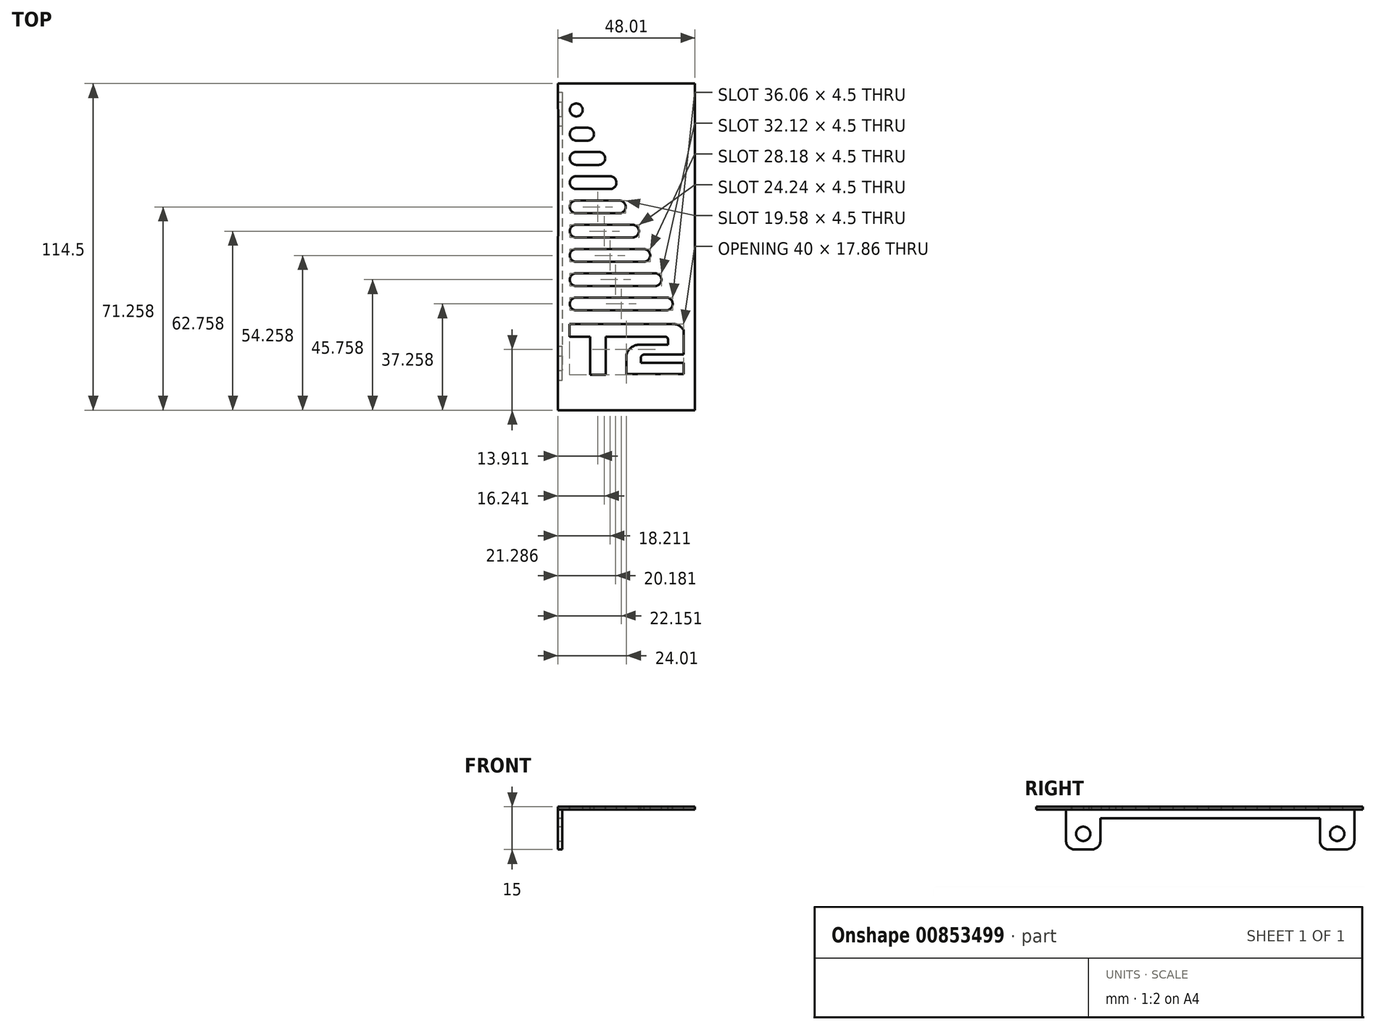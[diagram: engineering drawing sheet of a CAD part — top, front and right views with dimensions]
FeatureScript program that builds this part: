
annotation { "Feature Type Name" : "Feature", "Feature Type Description" : "" }
export const myFeature = defineFeature(function(context is Context, id is Id, definition is map)
    precondition{}
    {
        {
            var Q0;
            Q0=qCreatedBy(makeId("Top.planeOp"),FACE);
            var sketch = newSketch(context, id + "F0", { "sketchPlane" : qUnion([Q0])});
            skLineSegment(sketch, "E0.bottom", {"start": v(-24, 57.25) * mm, "end": v(24, 57.25) * mm});
            skLineSegment(sketch, "E0.right", {"start": v(24, 57.25) * mm, "end": v(24, -57.25) * mm});
            skPoint(sketch, "E0.middle", {"position": v(0, 0) * mm});
            skLineSegment(sketch, "E1", {"start": v(-20, -27.03) * mm, "end": v(-20, -31.53) * mm});
            skLineSegment(sketch, "E2", {"start": v(-12.75, -31.53) * mm, "end": v(-20, -31.53) * mm});
            skLineSegment(sketch, "E3", {"start": v(-12.75, -31.53) * mm, "end": v(-12.75, -44.9) * mm});
            skLineSegment(sketch, "E4", {"start": v(-12.75, -44.9) * mm, "end": v(-7.25, -44.9) * mm});
            skLineSegment(sketch, "E5", {"start": v(19.99, -40.62) * mm, "end": v(4.99, -40.62) * mm});
            skArc(sketch, "E6", {"start": v(4.33, -34.3) * mm, "mid": v(1.6, -35.34) * mm, "end": v(0, -37.8) * mm});
            skArc(sketch, "E7", {"start": v(6.16, -37.76) * mm, "mid": v(5.44, -38.04) * mm, "end": v(4.99, -38.66) * mm});
            skArc(sketch, "E8", {"start": v(20, -29.26) * mm, "mid": v(18.38, -27.56) * mm, "end": v(16.1, -27.03) * mm});
            skLineSegment(sketch, "E9", {"start": v(-20, -27.03) * mm, "end": v(16.1, -27.03) * mm});
            skLineSegment(sketch, "E10", {"start": v(4.99, -38.66) * mm, "end": v(4.99, -40.62) * mm});
            skLineSegment(sketch, "E11", {"start": v(6.16, -37.76) * mm, "end": v(20, -37.76) * mm});
            skLineSegment(sketch, "E12", {"start": v(20, -29.26) * mm, "end": v(20, -37.76) * mm});
            skLineSegment(sketch, "E13", {"start": v(4.33, -34.3) * mm, "end": v(14.5, -34.3) * mm});
            skLineSegment(sketch, "E14", {"start": v(-17.64, -22.24) * mm, "end": v(13.92, -22.24) * mm});
            skLineSegment(sketch, "E15", {"start": v(13.92, -17.74) * mm, "end": v(-17.64, -17.74) * mm});
            skArc(sketch, "E16", {"start": v(-17.64, -17.74) * mm, "mid": v(-19.89, -20) * mm, "end": v(-17.64, -22.24) * mm});
            skArc(sketch, "E17", {"start": v(13.92, -17.74) * mm, "mid": v(16.17, -20) * mm, "end": v(13.92, -22.24) * mm});
            skLineSegment(sketch, "E18", {"start": v(-17.64, -13.74) * mm, "end": v(9.98, -13.74) * mm});
            skLineSegment(sketch, "E19", {"start": v(9.98, -9.24) * mm, "end": v(-17.64, -9.24) * mm});
            skArc(sketch, "E20", {"start": v(-17.64, -9.24) * mm, "mid": v(-19.89, -11.5) * mm, "end": v(-17.64, -13.74) * mm});
            skArc(sketch, "E21", {"start": v(9.98, -9.24) * mm, "mid": v(12.23, -11.5) * mm, "end": v(9.98, -13.74) * mm});
            skLineSegment(sketch, "E22", {"start": v(-17.64, -5.24) * mm, "end": v(6.04, -5.24) * mm});
            skLineSegment(sketch, "E23", {"start": v(6.04, -0.74) * mm, "end": v(-17.64, -0.74) * mm});
            skArc(sketch, "E24", {"start": v(-17.64, -0.74) * mm, "mid": v(-19.89, -3) * mm, "end": v(-17.64, -5.24) * mm});
            skArc(sketch, "E25", {"start": v(6.04, -0.74) * mm, "mid": v(8.3, -3) * mm, "end": v(6.04, -5.24) * mm});
            skLineSegment(sketch, "E26", {"start": v(-17.64, 3.26) * mm, "end": v(2.1, 3.26) * mm});
            skLineSegment(sketch, "E27", {"start": v(2.1, 7.76) * mm, "end": v(-17.64, 7.76) * mm});
            skArc(sketch, "E28", {"start": v(-17.64, 7.76) * mm, "mid": v(-19.89, 5.5) * mm, "end": v(-17.64, 3.26) * mm});
            skArc(sketch, "E29", {"start": v(2.1, 7.76) * mm, "mid": v(4.35, 5.5) * mm, "end": v(2.1, 3.26) * mm});
            skLineSegment(sketch, "E30", {"start": v(-17.64, 11.76) * mm, "end": v(-2.56, 11.76) * mm});
            skLineSegment(sketch, "E31", {"start": v(-2.56, 16.26) * mm, "end": v(-17.64, 16.26) * mm});
            skArc(sketch, "E32", {"start": v(-17.64, 16.26) * mm, "mid": v(-19.89, 14) * mm, "end": v(-17.64, 11.76) * mm});
            skArc(sketch, "E33", {"start": v(-2.56, 16.26) * mm, "mid": v(-0.3, 14) * mm, "end": v(-2.56, 11.76) * mm});
            skLineSegment(sketch, "E34", {"start": v(-17.64, 20.26) * mm, "end": v(-5.78, 20.26) * mm});
            skLineSegment(sketch, "E35", {"start": v(-5.78, 24.76) * mm, "end": v(-17.64, 24.76) * mm});
            skArc(sketch, "E36", {"start": v(-17.64, 24.76) * mm, "mid": v(-19.89, 22.5) * mm, "end": v(-17.64, 20.26) * mm});
            skArc(sketch, "E37", {"start": v(-5.78, 24.76) * mm, "mid": v(-3.53, 22.5) * mm, "end": v(-5.78, 20.26) * mm});
            skLineSegment(sketch, "E38", {"start": v(-17.64, 28.76) * mm, "end": v(-9.72, 28.76) * mm});
            skLineSegment(sketch, "E39", {"start": v(-9.72, 33.26) * mm, "end": v(-17.64, 33.26) * mm});
            skArc(sketch, "E40", {"start": v(-17.64, 33.26) * mm, "mid": v(-19.89, 31) * mm, "end": v(-17.64, 28.76) * mm});
            skArc(sketch, "E41", {"start": v(-9.72, 33.26) * mm, "mid": v(-7.47, 31) * mm, "end": v(-9.72, 28.76) * mm});
            skLineSegment(sketch, "E42", {"start": v(-17.64, 37.26) * mm, "end": v(-13.66, 37.26) * mm});
            skLineSegment(sketch, "E43", {"start": v(-13.66, 41.76) * mm, "end": v(-17.64, 41.76) * mm});
            skArc(sketch, "E44", {"start": v(-17.64, 41.76) * mm, "mid": v(-19.89, 39.5) * mm, "end": v(-17.64, 37.26) * mm});
            skArc(sketch, "E45", {"start": v(-13.66, 41.76) * mm, "mid": v(-11.4, 39.5) * mm, "end": v(-13.66, 37.26) * mm});
            skLineSegment(sketch, "E46", {"start": v(-17.64, 45.76) * mm, "end": v(-17.6, 45.76) * mm});
            skLineSegment(sketch, "E47", {"start": v(-17.6, 50.26) * mm, "end": v(-17.64, 50.26) * mm});
            skArc(sketch, "E48", {"start": v(-17.64, 50.26) * mm, "mid": v(-19.89, 48) * mm, "end": v(-17.64, 45.76) * mm});
            skArc(sketch, "E49", {"start": v(-17.6, 50.26) * mm, "mid": v(-15.35, 48) * mm, "end": v(-17.6, 45.76) * mm});
            skLineSegment(sketch, "E50", {"start": v(-7.25, -44.9) * mm, "end": v(-7.25, -31.53) * mm});
            skLineSegment(sketch, "E51", {"start": v(19.99, -40.62) * mm, "end": v(20, -44.62) * mm});
            skLineSegment(sketch, "E52", {"start": v(0, -37.8) * mm, "end": v(0, -44.62) * mm});
            skLineSegment(sketch, "E53", {"start": v(0, -44.62) * mm, "end": v(20, -44.62) * mm});
            skArc(sketch, "E54", {"start": v(14.5, -32.31) * mm, "mid": v(14.27, -31.76) * mm, "end": v(13.72, -31.53) * mm});
            skLineSegment(sketch, "E55", {"start": v(14.5, -32.31) * mm, "end": v(14.5, -34.3) * mm});
            skLineSegment(sketch, "E56", {"start": v(-7.25, -31.53) * mm, "end": v(13.72, -31.53) * mm});
            skLineSegment(sketch, "E57", {"start": v(-24, -57.25) * mm, "end": v(24, -57.25) * mm});
            skLineSegment(sketch, "E58", {"start": v(-24, 57.25) * mm, "end": v(-24, 54.25) * mm});
            skLineSegment(sketch, "E59", {"start": v(-24, 54.25) * mm, "end": v(-22.5, 54.25) * mm});
            skLineSegment(sketch, "E60", {"start": v(-22.5, 54.25) * mm, "end": v(-22.5, 42.25) * mm});
            skLineSegment(sketch, "E61", {"start": v(-22.5, 42.25) * mm, "end": v(-23.94, 42.25) * mm});
            skPoint(sketch, "E62", {"position": v(-24, -46.75) * mm});
            skLineSegment(sketch, "E63", {"start": v(-24, -46.75) * mm, "end": v(-22.5, -46.75) * mm});
            skLineSegment(sketch, "E64", {"start": v(-22.5, -46.75) * mm, "end": v(-22.5, -34.75) * mm});
            skLineSegment(sketch, "E65", {"start": v(-24, -46.75) * mm, "end": v(-24, -34.75) * mm});
            skLineSegment(sketch, "E66", {"start": v(-24, -34.75) * mm, "end": v(-22.5, -34.75) * mm});
            skLineSegment(sketch, "E67", {"start": v(-24, -57.25) * mm, "end": v(-24, -46.75) * mm});
            skLineSegment(sketch, "E68", {"start": v(-24, 54.25) * mm, "end": v(-23.94, 42.25) * mm});
            skLineSegment(sketch, "E69", {"start": v(-23.94, 42.25) * mm, "end": v(-24, -34.75) * mm});
            skLineSegment(sketch, "E70", {"start": v(-22.5, 42.25) * mm, "end": v(-22.5, -34.75) * mm});
            skSolve(sketch);
        }
        {
            var Q0;
            Q0=makeQuery(id+"F0.imprint","IMPRINT",FACE,{"disambiguationData":[TD([[makeQuery(id+"F0.imprint","IMPRINT",EDGE,{"derivedFrom":sQuery(id+"F0.wireOp",EDGE,"E0.bottom")}),-1.0]])]});
            extrude(context, id + "F1", {"entities" : qUnion([Q0]), "oppositeDirection" : true, "depth" : 1 * mm, "offsetDistance" : 25 * mm});
        }
        {
            var Q0;
            Q0=makeQuery(id+"F0.imprint","IMPRINT",FACE,{"disambiguationData":[TD([[makeQuery(id+"F0.imprint","IMPRINT",EDGE,{"derivedFrom":sQuery(id+"F0.wireOp",EDGE,"E59")}),-1.0]])]});
            var Q1;
            Q1=makeQuery(id+"F0.imprint","IMPRINT",FACE,{"disambiguationData":[TD([[makeQuery(id+"F0.imprint","IMPRINT",EDGE,{"derivedFrom":sQuery(id+"F0.wireOp",EDGE,"E63")}),1.0]])]});
            extrude(context, id + "F2", {"entities" : qUnion([Q0, Q1]), "operationType" : NewBodyOperationType.ADD, "oppositeDirection" : true, "depth" : 15 * mm, "offsetDistance" : 25 * mm});
        }
        {
            var Q0;
            Q0=qCreatedBy(makeId("Right.planeOp"),FACE);
            var sketch = newSketch(context, id + "F3", { "sketchPlane" : qUnion([Q0])});
            skPoint(sketch, "E71", {"position": v(-40.75, -9.5) * mm});
            skPoint(sketch, "E72", {"position": v(48.25, -9.5) * mm});
            skSolve(sketch);
        }
        {
            var Q0;
            Q0=sQuery(id+"F3.wireOp",VERTEX,"E71");
            var Q1;
            Q1=sQuery(id+"F3.wireOp",VERTEX,"E72");
            var Q2;
            Q2=makeQuery(id+"F1.opExtrude","SWEPT_BODY",BODY,{"disambiguationData":[OSD([sQuery(id+"F0.wireOp",EDGE,"E0.bottom"),sQuery(id+"F0.wireOp",EDGE,"E0.top"),sQuery(id+"F0.wireOp",EDGE,"E0.right"),sQuery(id+"F0.wireOp",EDGE,"E1"),sQuery(id+"F0.wireOp",EDGE,"E2"),sQuery(id+"F0.wireOp",EDGE,"E3"),sQuery(id+"F0.wireOp",EDGE,"E4"),sQuery(id+"F0.wireOp",EDGE,"0LANiQkd-xG1w-0jAY-0H3d-zRR3qAL3rn1X"),sQuery(id+"F0.wireOp",EDGE,"E5"),sQuery(id+"F0.wireOp",EDGE,"E6"),sQuery(id+"F0.wireOp",EDGE,"E7"),sQuery(id+"F0.wireOp",EDGE,"E8"),sQuery(id+"F0.wireOp",EDGE,"E9"),sQuery(id+"F0.wireOp",EDGE,"E10"),sQuery(id+"F0.wireOp",EDGE,"E11"),sQuery(id+"F0.wireOp",EDGE,"E12"),sQuery(id+"F0.wireOp",EDGE,"E13"),sQuery(id+"F0.wireOp",EDGE,"H3LriEdK-IGWu-km3t-O8Rp-QvWeqxySHV8o"),sQuery(id+"F0.wireOp",EDGE,"EcIqTxym-PrgU-ehmv-7TEX-s5XfxjkhuH4a"),sQuery(id+"F0.wireOp",EDGE,"6be5b86a-f134-4340-a0f3-9762bb9dc0c5"),sQuery(id+"F0.wireOp",EDGE,"d7688d6a-630d-4f20-921e-fb5fbf414a30"),sQuery(id+"F0.wireOp",EDGE,"E14"),sQuery(id+"F0.wireOp",EDGE,"E15"),sQuery(id+"F0.wireOp",EDGE,"E16"),sQuery(id+"F0.wireOp",EDGE,"E17"),sQuery(id+"F0.wireOp",EDGE,"E18"),sQuery(id+"F0.wireOp",EDGE,"E19"),sQuery(id+"F0.wireOp",EDGE,"E20"),sQuery(id+"F0.wireOp",EDGE,"E21"),sQuery(id+"F0.wireOp",EDGE,"E22"),sQuery(id+"F0.wireOp",EDGE,"E23"),sQuery(id+"F0.wireOp",EDGE,"E24"),sQuery(id+"F0.wireOp",EDGE,"E25"),sQuery(id+"F0.wireOp",EDGE,"E26"),sQuery(id+"F0.wireOp",EDGE,"E27"),sQuery(id+"F0.wireOp",EDGE,"E28"),sQuery(id+"F0.wireOp",EDGE,"E29"),sQuery(id+"F0.wireOp",EDGE,"E30"),sQuery(id+"F0.wireOp",EDGE,"E31"),sQuery(id+"F0.wireOp",EDGE,"E32"),sQuery(id+"F0.wireOp",EDGE,"E33"),sQuery(id+"F0.wireOp",EDGE,"E34"),sQuery(id+"F0.wireOp",EDGE,"E35"),sQuery(id+"F0.wireOp",EDGE,"E36"),sQuery(id+"F0.wireOp",EDGE,"E37"),sQuery(id+"F0.wireOp",EDGE,"E38"),sQuery(id+"F0.wireOp",EDGE,"E39"),sQuery(id+"F0.wireOp",EDGE,"E40"),sQuery(id+"F0.wireOp",EDGE,"E41"),sQuery(id+"F0.wireOp",EDGE,"E42"),sQuery(id+"F0.wireOp",EDGE,"E43"),sQuery(id+"F0.wireOp",EDGE,"E44"),sQuery(id+"F0.wireOp",EDGE,"E45"),sQuery(id+"F0.wireOp",EDGE,"E46"),sQuery(id+"F0.wireOp",EDGE,"E47"),sQuery(id+"F0.wireOp",EDGE,"E48"),sQuery(id+"F0.wireOp",EDGE,"E49"),sQuery(id+"F0.wireOp",EDGE,"E50"),sQuery(id+"F0.wireOp",EDGE,"E51"),sQuery(id+"F0.wireOp",EDGE,"E52"),sQuery(id+"F0.wireOp",EDGE,"E53"),sQuery(id+"F0.wireOp",EDGE,"E54"),sQuery(id+"F0.wireOp",EDGE,"E55"),sQuery(id+"F0.wireOp",EDGE,"E56")])]});
            hole(context, id + "F4", {"style" : HoleStyle.SIMPLE, "endStyle" : HoleEndStyle.THROUGH, "holeDiameter" : 5 * mm, "majorDiameter" : 5 * mm, "isTappedThrough" : true, "tappedDepth" : 12 * mm, "tapClearance" : 3, "locations" : qUnion([Q0, Q1]), "scope" : qUnion([Q2])});
        }
        {
            var Q0;
            Q0=makeQuery(id+"F2.opExtrude","CAP_EDGE",EDGE,{"disambiguationData":[OSD([sQuery(id+"F0.wireOp",EDGE,"HBLAxpmw-sJ8A-g88T-pWDY-p4oM08mXjc2A")])],"isStart":false});
            var Q1;
            Q1=makeQuery(id+"F2.opExtrude","CAP_EDGE",EDGE,{"disambiguationData":[OSD([sQuery(id+"F0.wireOp",EDGE,"E61")])],"isStart":false});
            var Q2;
            Q2=makeQuery(id+"F2.opExtrude","CAP_EDGE",EDGE,{"disambiguationData":[OSD([sQuery(id+"F0.wireOp",EDGE,"E59")])],"isStart":false});
            var Q3;
            Q3=makeQuery(id+"F2.opExtrude","CAP_EDGE",EDGE,{"disambiguationData":[OSD([sQuery(id+"F0.wireOp",EDGE,"z9CvzlAU-oE5h-fNBz-gN4p-R0uBhrxic2hj")])],"isStart":false});
            var Q4;
            Q4=makeQuery(id+"F2.opExtrude","CAP_EDGE",EDGE,{"disambiguationData":[OSD([sQuery(id+"F0.wireOp",EDGE,"E66")])],"isStart":false});
            var Q5;
            Q5=makeQuery(id+"F2.opExtrude","CAP_EDGE",EDGE,{"disambiguationData":[OSD([sQuery(id+"F0.wireOp",EDGE,"E63")])],"isStart":false});
            fillet(context, id + "F5", {"entities" : qUnion([Q0, Q1, Q2, Q3, Q4, Q5]), "radius" : 3 * mm, "tangentPropagation" : true, "allowEdgeOverflow" : false});
        }
        {
            var Q0;
            Q0=makeQuery(id+"F0.imprint","IMPRINT",FACE,{"disambiguationData":[TD([[makeQuery(id+"F0.imprint","IMPRINT",EDGE,{"derivedFrom":sQuery(id+"F0.wireOp",EDGE,"E61")}),1.0]])]});
            extrude(context, id + "F6", {"entities" : qUnion([Q0]), "operationType" : NewBodyOperationType.ADD, "oppositeDirection" : true, "depth" : 4 * mm, "offsetDistance" : 25 * mm});
        }
    });
